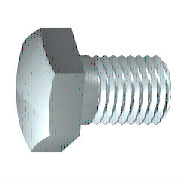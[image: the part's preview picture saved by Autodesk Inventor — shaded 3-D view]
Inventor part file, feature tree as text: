
AUTODESK INVENTOR PART (.ipt)
format: ipt  version: 2020 (Build 240168000, 168)  size: 192,000 bytes
history: native  units: mm (DEFAULTED — no unit token found)
features: sketch x3, extrude x1, chamfer x1, plane x1
ambient origin geometry x7: Origin, YZ Plane, XZ Plane, X Axis, Y Axis, Z Axis, Center Point
bodies: Solid1 (feature_tree), Body (feature_tree)
feature tree (6):
  extrude  "Head"  Depth=37.9mm
  chamfer  "Chamfer1"  Distance=2.4mm
  plane  "Work Plane1"
  sketch  "Sketch1"  dims[d0=40.0mm d1=37.9mm]
  sketch  "Sketch2"  dims[d2=4.0mm]
  sketch  "Sketch4"  dims[d12=90.0deg d3=2.4mm d4=0.0mm d5=30.0deg d21=90.0deg d6=0.429415mm d7=0.429515mm d8=0.0mm d9=0.4001mm d10=5.88mm d11=7.0mm d13=0.429515mm d14=4.0mm d15=37.9mm d16=0.0mm d19=7.0mm d55=45.0deg d57=0.0mm d58=0.0mm]
